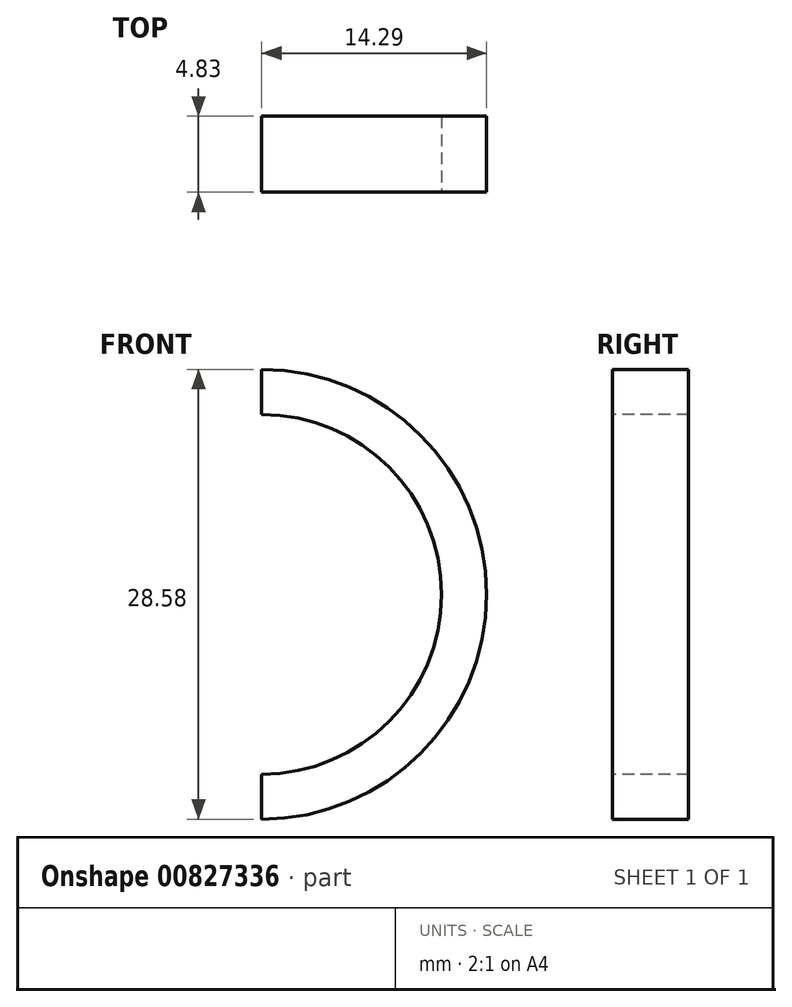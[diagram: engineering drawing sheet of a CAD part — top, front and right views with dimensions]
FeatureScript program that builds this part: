
annotation { "Feature Type Name" : "Feature", "Feature Type Description" : "" }
export const myFeature = defineFeature(function(context is Context, id is Id, definition is map)
    precondition{}
    {
        {
            var Q0;
            Q0=qCreatedBy(makeId("Front.planeOp"),FACE);
            var sketch = newSketch(context, id + "F0", { "sketchPlane" : qUnion([Q0])});
            skArc(sketch, "E0", {"start": v(0, -11.43) * mm, "mid": v(11.43, 0) * mm, "end": v(0, 11.43) * mm});
            skArc(sketch, "E1", {"start": v(0, -14.29) * mm, "mid": v(14.29, 0) * mm, "end": v(0, 14.29) * mm});
            skLineSegment(sketch, "E2", {"start": v(0, 14.29) * mm, "end": v(0, 11.43) * mm});
            skPoint(sketch, "E3.orphan", {"position": v(0, 17.52) * mm});
            skLineSegment(sketch, "E4.trimOffspring", {"start": v(0, -11.43) * mm, "end": v(0, -14.29) * mm});
            skSolve(sketch);
        }
        {
            var Q0;
            Q0=makeQuery(id+"F0.imprint","IMPRINT",FACE,{"disambiguationData":[TD([[makeQuery(id+"F0.imprint","IMPRINT",EDGE,{"derivedFrom":sQuery(id+"F0.wireOp",EDGE,"E0")}),-1.0]])]});
            extrude(context, id + "F1", {"entities" : qUnion([Q0]), "flatOperationType" : FlatOperationType.REMOVE, "oppositeDirection" : true, "depth" : 4.83 * mm, "offsetDistance" : 25.4 * mm, "domain" : OperationDomain.MODEL});
        }
    });
